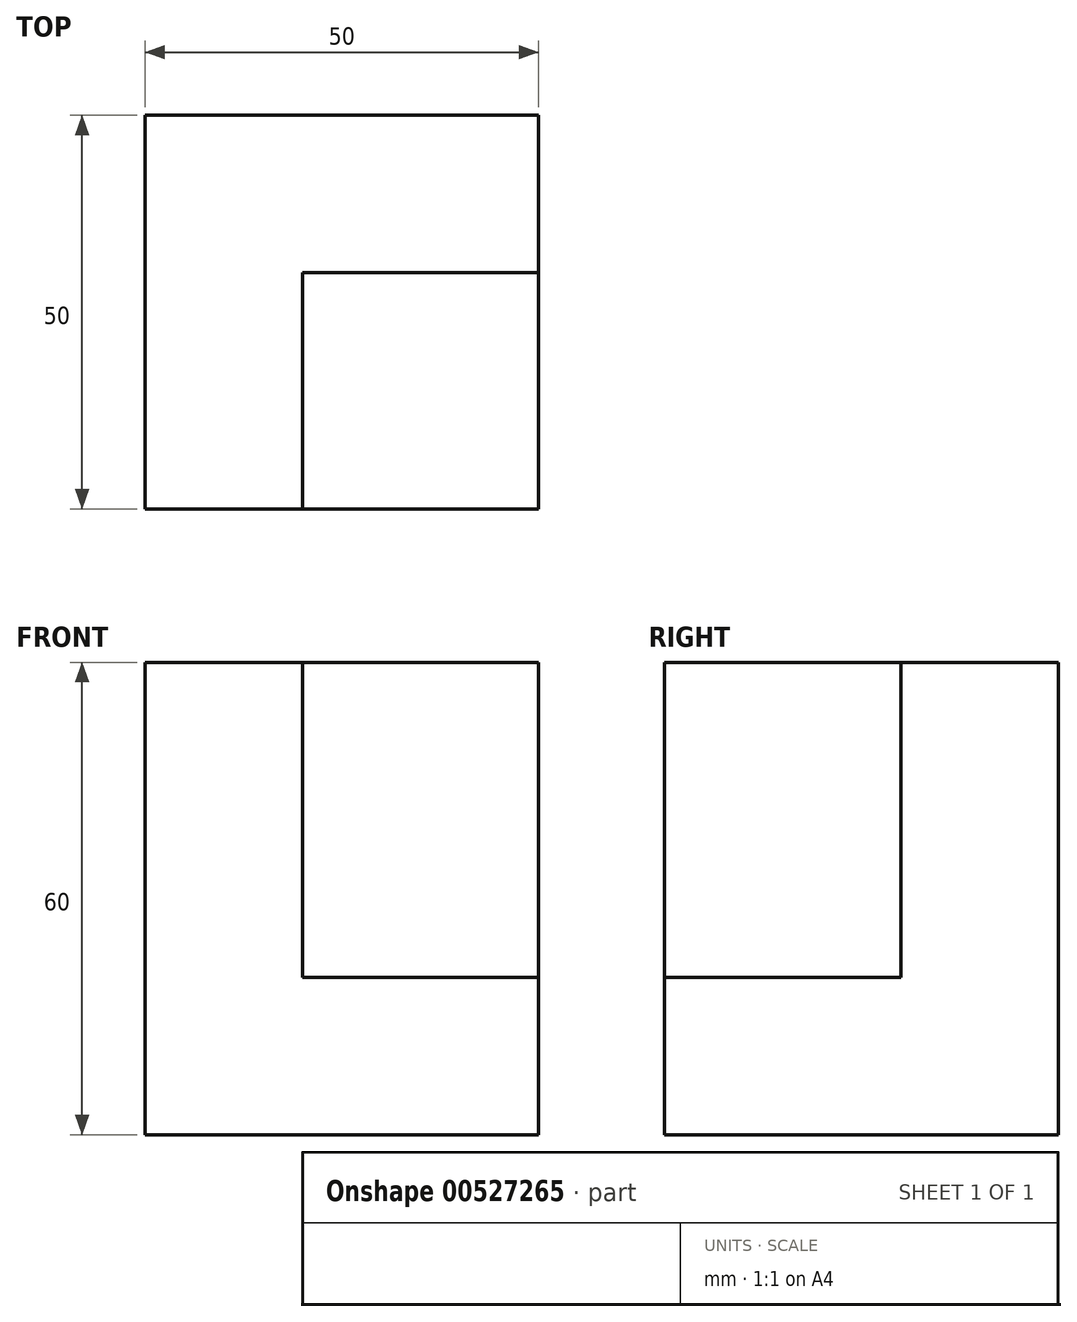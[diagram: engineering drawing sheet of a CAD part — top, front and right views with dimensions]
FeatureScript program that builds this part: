
annotation { "Feature Type Name" : "Feature", "Feature Type Description" : "" }
export const myFeature = defineFeature(function(context is Context, id is Id, definition is map)
    precondition{}
    {
        {
            var Q0;
            Q0=qCreatedBy(makeId("Front.planeOp"),FACE);
            var sketch = newSketch(context, id + "F0", { "sketchPlane" : qUnion([Q0])});
            skLineSegment(sketch, "E0", {"start": v(0, 0) * mm, "end": v(50, 0) * mm});
            skLineSegment(sketch, "E1", {"start": v(50, 0) * mm, "end": v(50, 20) * mm});
            skLineSegment(sketch, "E2", {"start": v(50, 20) * mm, "end": v(20, 20) * mm});
            skLineSegment(sketch, "E3", {"start": v(20, 20) * mm, "end": v(20, 60) * mm});
            skLineSegment(sketch, "E4", {"start": v(20, 60) * mm, "end": v(0, 60) * mm});
            skLineSegment(sketch, "E5", {"start": v(0, 60) * mm, "end": v(0, 0) * mm});
            skSolve(sketch);
        }
        {
            var Q0;
            Q0=qSketchRegion(id+"F0",true);
            extrude(context, id + "F1", {"entities" : qUnion([Q0]), "depth" : 50 * mm});
        }
        {
            var Q0;
            Q0=makeQuery(id+"F1.opExtrude","CAP_FACE",FACE,{"disambiguationData":[OSD([sQuery(id+"F0.wireOp",EDGE,"E0"),sQuery(id+"F0.wireOp",EDGE,"E1"),sQuery(id+"F0.wireOp",EDGE,"E2"),sQuery(id+"F0.wireOp",EDGE,"E3"),sQuery(id+"F0.wireOp",EDGE,"E4"),sQuery(id+"F0.wireOp",EDGE,"E5")])],"isStart":true});
            var sketch = newSketch(context, id + "F2", { "sketchPlane" : qUnion([Q0])});
            skLineSegment(sketch, "E6", {"start": v(-50, 20) * mm, "end": v(-50, 60) * mm});
            skLineSegment(sketch, "E7", {"start": v(-50, 60) * mm, "end": v(-20, 60) * mm});
            skLineSegment(sketch, "E8", {"start": v(-20, 60) * mm, "end": v(-20, 20) * mm});
            skLineSegment(sketch, "E9", {"start": v(-20, 20) * mm, "end": v(-50, 20) * mm});
            skSolve(sketch);
        }
        {
            var Q0;
            Q0=qSketchRegion(id+"F2",true);
            extrude(context, id + "F3", {"entities" : qUnion([Q0]), "operationType" : NewBodyOperationType.ADD, "oppositeDirection" : true, "depth" : 20 * mm});
        }
    });
